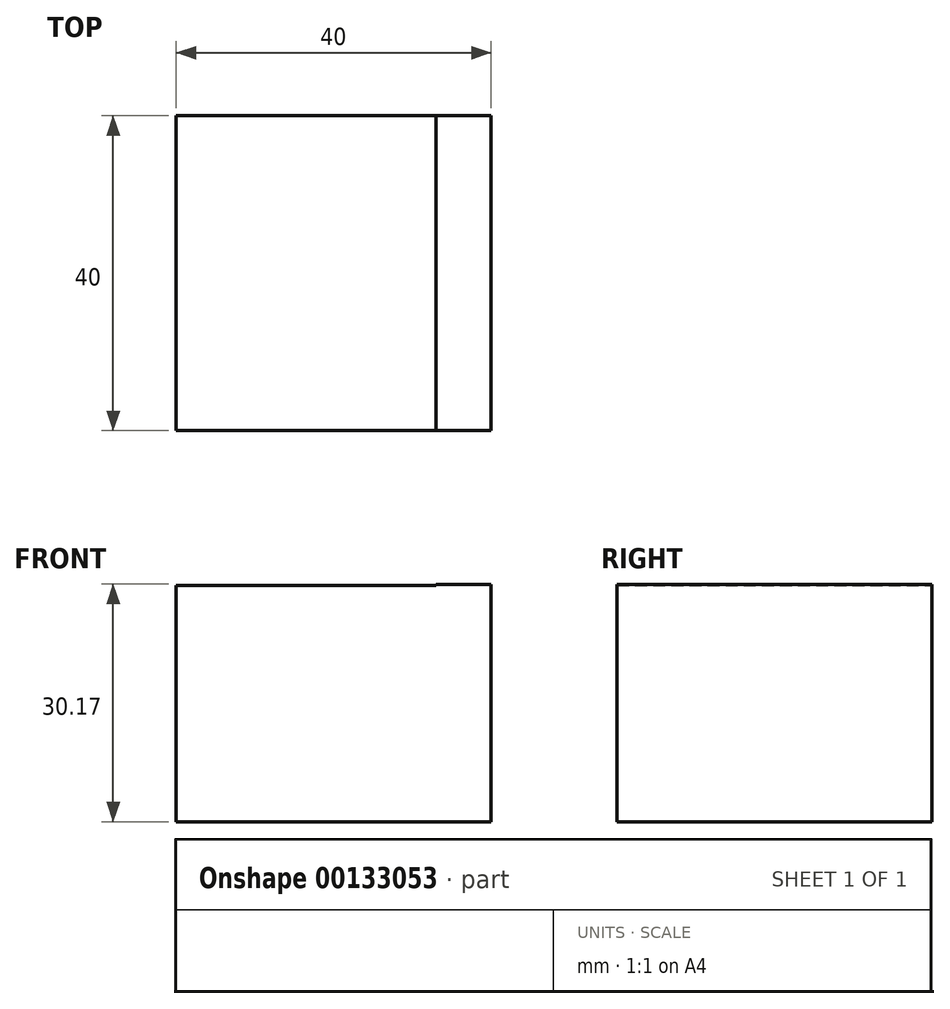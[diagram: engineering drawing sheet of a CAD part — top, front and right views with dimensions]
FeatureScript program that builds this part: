
annotation { "Feature Type Name" : "Feature", "Feature Type Description" : "" }
export const myFeature = defineFeature(function(context is Context, id is Id, definition is map)
    precondition{}
    {
        {
            var Q0;
            Q0=qCreatedBy(makeId("Front.planeOp"),FACE);
            var sketch = newSketch(context, id + "F0", { "sketchPlane" : qUnion([Q0])});
            skLineSegment(sketch, "E0.bottom", {"start": v(-32.06, 18.17) * mm, "end": v(-25.06, 18.17) * mm});
            skLineSegment(sketch, "E0.top", {"start": v(-32.06, -11.83) * mm, "end": v(-25.06, -11.83) * mm});
            skLineSegment(sketch, "E0.left", {"start": v(-32.06, 18.17) * mm, "end": v(-32.06, -11.83) * mm});
            skLineSegment(sketch, "E0.right", {"start": v(-25.06, 18.17) * mm, "end": v(-25.06, -11.83) * mm});
            skLineSegment(sketch, "E1.bottom", {"start": v(-25.06, -11.83) * mm, "end": v(0.94, -11.83) * mm});
            skLineSegment(sketch, "E1.top", {"start": v(-25.06, -4.83) * mm, "end": v(0.94, -4.83) * mm});
            skLineSegment(sketch, "E1.left", {"start": v(-25.06, -11.83) * mm, "end": v(-25.06, -4.83) * mm});
            skLineSegment(sketch, "E1.right", {"start": v(0.94, -11.83) * mm, "end": v(0.94, -4.83) * mm});
            skLineSegment(sketch, "E2.bottom", {"start": v(0.94, -11.83) * mm, "end": v(7.94, -11.83) * mm});
            skLineSegment(sketch, "E2.top", {"start": v(0.94, 18.34) * mm, "end": v(7.94, 18.34) * mm});
            skLineSegment(sketch, "E2.left", {"start": v(0.94, -11.83) * mm, "end": v(0.94, 18.34) * mm});
            skLineSegment(sketch, "E2.right", {"start": v(7.94, -11.83) * mm, "end": v(7.94, 18.34) * mm});
            skLineSegment(sketch, "E3.bottom", {"start": v(-25.06, 18.17) * mm, "end": v(0.94, 18.17) * mm});
            skLineSegment(sketch, "E3.left", {"start": v(-25.06, 18.17) * mm, "end": v(-25.06, -4.83) * mm});
            skLineSegment(sketch, "E3.right", {"start": v(0.94, 18.17) * mm, "end": v(0.94, -4.83) * mm});
            skSolve(sketch);
        }
        {
            var Q0;
            Q0 = qSketchRegion(id + "F0", true);
            extrude(context, id + "F1", {"entities" : qUnion([Q0]), "endBound" : BoundingType.SYMMETRIC, "depth" : 40 * mm});
        }
    });
